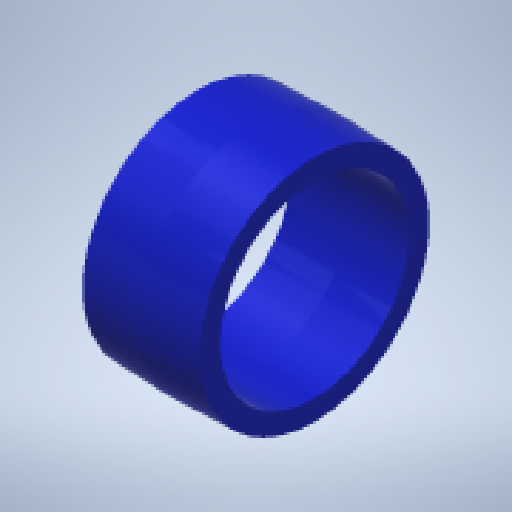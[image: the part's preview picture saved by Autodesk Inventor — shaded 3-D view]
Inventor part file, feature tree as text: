
AUTODESK INVENTOR PART (.ipt)
format: ipt  version: 2023 (Build 270158000, 158)  size: 144,384 bytes
history: native  units: in
note: dims shown in document units (in); Inventor stores cm internally (conversion verified against a paired STEP export)
features: revolve x1
ambient origin geometry x8: Origin, YZ Plane, XZ Plane, XY Plane, X Axis, Y Axis, Z Axis, Center Point
bodies: Solid1 (feature_tree)
feature tree (1):
  revolve  "Revolve1"  [1 undecoded]
note: 1 required parameter value undecoded (feature->parameter linkage not recoverable at this tier; creation-order binding heuristic only, values carry confidence <= 0.55)
